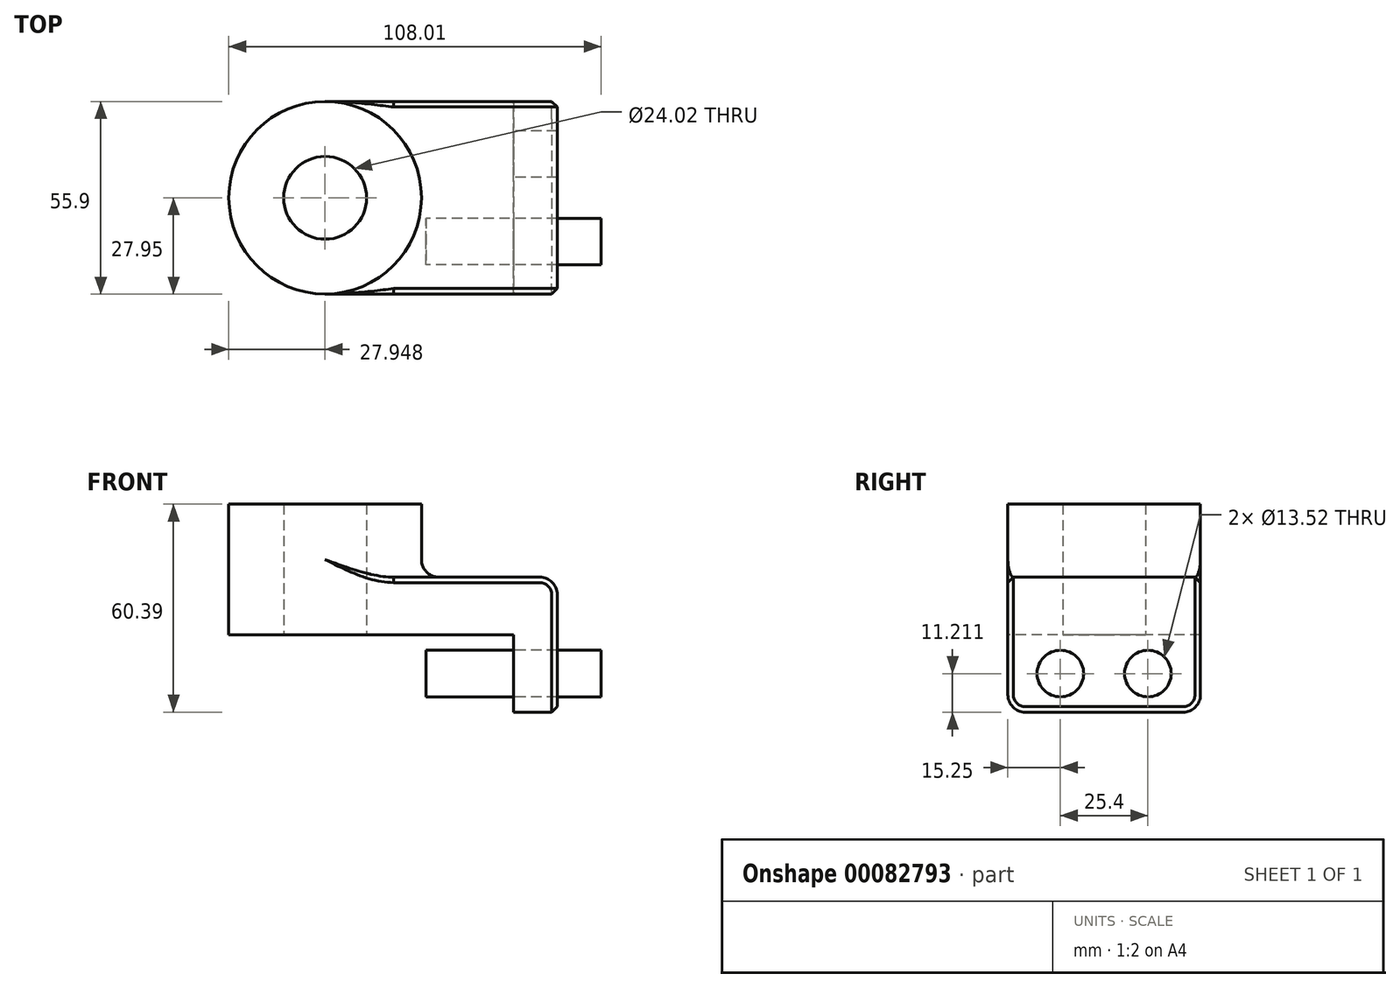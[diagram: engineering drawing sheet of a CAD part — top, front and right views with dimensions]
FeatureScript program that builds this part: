
annotation { "Feature Type Name" : "Feature", "Feature Type Description" : "" }
export const myFeature = defineFeature(function(context is Context, id is Id, definition is map)
    precondition{}
    {
        {
            var Q0;
            Q0=qCreatedBy(makeId("Top.planeOp"),FACE);
            var sketch = newSketch(context, id + "F0", { "sketchPlane" : qUnion([Q0])});
            skLineSegment(sketch, "E0.bottom", {"start": v(-27.33, 27.95) * mm, "end": v(27.33, 27.95) * mm});
            skLineSegment(sketch, "E0.top", {"start": v(-27.33, -27.95) * mm, "end": v(27.33, -27.95) * mm});
            skLineSegment(sketch, "E0.left", {"start": v(-27.33, 27.95) * mm, "end": v(-27.33, -27.95) * mm});
            skLineSegment(sketch, "E0.right", {"start": v(27.33, 27.95) * mm, "end": v(27.33, -27.95) * mm});
            skPoint(sketch, "E0.middle", {"position": v(0, 0) * mm});
            skCircle(sketch, "E1", {"center": v(-27.33, 0) * mm, "radius": 27.95 * mm});
            skCircle(sketch, "E2", {"center": v(-27.33, 0) * mm, "radius": 12 * mm});
            skSolve(sketch);
        }
        {
            var Q0;
            {var subQ1=sQuery(id+"F0.wireOp",EDGE,"E0.left");var subQ3=sQuery(id+"F0.wireOp",EDGE,"E2");var subQ4=makeQuery(id+"F0.imprint","INTERSECT",VERTEX,{"disambiguationData":[OD(0.0)],"derivedFrom":[subQ1,subQ3]});Q0=makeQuery(id+"F0.imprint","IMPRINT",FACE,{"disambiguationData":[TD([[makeQuery(id+"F0.imprint","IMPRINT",EDGE,{"disambiguationData":[TD([[subQ4,-1.0]])],"derivedFrom":subQ3}),-1.0]])]});}
            var Q1;
            {var subQ1=sQuery(id+"F0.wireOp",EDGE,"E0.left");var subQ3=sQuery(id+"F0.wireOp",EDGE,"E2");var subQ4=makeQuery(id+"F0.imprint","INTERSECT",VERTEX,{"disambiguationData":[OD(0.0)],"derivedFrom":[subQ1,subQ3]});Q1=makeQuery(id+"F0.imprint","IMPRINT",FACE,{"disambiguationData":[TD([[makeQuery(id+"F0.imprint","IMPRINT",EDGE,{"disambiguationData":[TD([[subQ4,1.0]])],"derivedFrom":subQ3}),-1.0]])]});}
            var Q2;
            {var subQ0=sQuery(id+"F0.wireOp",EDGE,"E0.bottom");Q2=makeQuery(id+"F0.imprint","IMPRINT",FACE,{"disambiguationData":[TD([[makeQuery(id+"F0.imprint","IMPRINT",EDGE,{"derivedFrom":subQ0}),-1.0]])]});}
            extrude(context, id + "F1", {"entities" : qUnion([Q0, Q1, Q2]), "depth" : 16.73 * mm});
        }
        {
            var Q0;
            {var subQ1=sQuery(id+"F0.wireOp",EDGE,"E0.left");var subQ3=sQuery(id+"F0.wireOp",EDGE,"E2");var subQ4=makeQuery(id+"F0.imprint","INTERSECT",VERTEX,{"disambiguationData":[OD(0.0)],"derivedFrom":[subQ1,subQ3]});Q0=makeQuery(id+"F0.imprint","IMPRINT",FACE,{"disambiguationData":[TD([[makeQuery(id+"F0.imprint","IMPRINT",EDGE,{"disambiguationData":[TD([[subQ4,-1.0]])],"derivedFrom":subQ3}),-1.0]])]});}
            var Q1;
            {var subQ1=sQuery(id+"F0.wireOp",EDGE,"E0.left");var subQ3=sQuery(id+"F0.wireOp",EDGE,"E2");var subQ4=makeQuery(id+"F0.imprint","INTERSECT",VERTEX,{"disambiguationData":[OD(0.0)],"derivedFrom":[subQ1,subQ3]});Q1=makeQuery(id+"F0.imprint","IMPRINT",FACE,{"disambiguationData":[TD([[makeQuery(id+"F0.imprint","IMPRINT",EDGE,{"disambiguationData":[TD([[subQ4,1.0]])],"derivedFrom":subQ3}),-1.0]])]});}
            extrude(context, id + "F2", {"entities" : qUnion([Q0, Q1]), "operationType" : NewBodyOperationType.ADD, "depth" : 37.92 * mm});
        }
        {
            var Q0;
            Q0=makeQuery(id+"F1.opExtrude","SWEPT_FACE",FACE,{"disambiguationData":[OSD([sQuery(id+"F0.wireOp",EDGE,"E0.right")])]});
            var sketch = newSketch(context, id + "F3", { "sketchPlane" : qUnion([Q0])});
            skLineSegment(sketch, "E3.bottom", {"start": v(-27.95, 16.73) * mm, "end": v(27.95, 16.73) * mm});
            skLineSegment(sketch, "E3.top", {"start": v(-27.95, -22.47) * mm, "end": v(27.95, -22.47) * mm});
            skLineSegment(sketch, "E3.left", {"start": v(-27.95, 16.73) * mm, "end": v(-27.95, -22.47) * mm});
            skLineSegment(sketch, "E3.right", {"start": v(27.95, 16.73) * mm, "end": v(27.95, -22.47) * mm});
            skCircle(sketch, "E4", {"center": v(-12.7, -11.26) * mm, "radius": 6.76 * mm});
            skLineSegment(sketch, "E5", {"start": v(0, 0) * mm, "end": v(0, -22.47) * mm, "construction": true});
            skCircle(sketch, "E6.MirrorC", {"center": v(12.7, -11.26) * mm, "radius": 6.76 * mm});
            skSolve(sketch);
        }
        {
            var Q0;
            Q0 = qSketchRegion(id + "F3", true);
            extrude(context, id + "F4", {"entities" : qUnion([Q0]), "operationType" : NewBodyOperationType.ADD, "depth" : 12.7 * mm});
        }
        {
            var Q0;
            {var subQ0=sQuery(id+"F0.wireOp",EDGE,"E1");Q0=makeQuery(id+"F2.boolean.opBoolean","INTERSECT",EDGE,{"derivedFrom":[makeQuery(id+"F1.opExtrude","CAP_FACE",FACE,{"disambiguationData":[OSD([sQuery(id+"F0.wireOp",EDGE,"E0.bottom"),sQuery(id+"F0.wireOp",EDGE,"E0.top"),sQuery(id+"F0.wireOp",EDGE,"E0.right"),subQ0,sQuery(id+"F0.wireOp",EDGE,"E2")])],"isStart":false}),makeQuery(id+"F2.opExtrude","SWEPT_FACE",FACE,{"disambiguationData":[OSD([subQ0])]})]});}
            var Q1;
            Q1=makeQuery(id+"F4.opExtrude","CAP_EDGE",EDGE,{"disambiguationData":[OSD([sQuery(id+"F3.wireOp",EDGE,"E3.bottom")])],"isStart":false});
            var Q2;
            Q2=makeQuery(id+"F4.opExtrude","SWEPT_EDGE",EDGE,{"disambiguationData":[OSD([sQuery(id+"F3.wireOp",EDGE,"E3.top"),sQuery(id+"F3.wireOp",EDGE,"E3.left")])]});
            var Q3;
            Q3=makeQuery(id+"F4.opExtrude","SWEPT_EDGE",EDGE,{"disambiguationData":[OSD([sQuery(id+"F3.wireOp",EDGE,"E3.top"),sQuery(id+"F3.wireOp",EDGE,"E3.right")])]});
            fillet(context, id + "F5", {"entities" : qUnion([Q0, Q1, Q2, Q3]), "radius" : 5.08 * mm, "tangentPropagation" : true, "allowEdgeOverflow" : false});
        }
        {
            var Q0;
            Q0=makeQuery(id+"F4.opExtrude","CAP_EDGE",EDGE,{"disambiguationData":[OSD([sQuery(id+"F3.wireOp",EDGE,"E3.right")])],"isStart":false});
            chamfer(context, id + "F6", {"entities" : qUnion([Q0]), "width" : 1.59 * mm, "tangentPropagation" : true});
        }
        {
            var Q0;
            Q0=makeQuery(id+"F3.imprint","IMPRINT",FACE,{"disambiguationData":[TD([[makeQuery(id+"F3.imprint","IMPRINT",EDGE,{"derivedFrom":sQuery(id+"F3.wireOp",EDGE,"E4")}),1.0]])]});
            extrude(context, id + "F7", {"entities" : qUnion([Q0]), "depth" : 25.4 * mm, "hasSecondDirection" : true, "secondDirectionOppositeDirection" : true, "secondDirectionDepth" : 25.4 * mm});
        }
    });
